# Revit family: Скамейка стальная круглая «Радиус Раунд» без спинки Арт 22157
name_source: partatom
category: Антураж
revit_build: Autodesk Revit 2018 (Build: 20180423_1000(x64)
units: mm (PartAtom-declared; Revit-internal decimal feet)

## family parameters
Всегда вертикально = Да
Источник визуального образа = Геометрия семейства
На основе рабочей плоскости = Нет
Общий = Нет
При загрузке вырезать с полостями = Нет
Точка расчета площади = Нет

## types (2) — shared parameters
URL = https://hobbyka.ru
Артикул товара = Арт. 22157
Высота = 450 мм
Группа модели = Скамейки
Изготовитель = ООО «Хоббика»
Изображение типоразмера = Скамейка стальная круглая «Радиус Раунд» без спинки Арт 22157.jpg
Материал изделия = Сталь, дерево
Цвет основания = Сталь
Цвет отделки = Дерево
Ширина = 500 мм

## per-type parameters (varying)
| type | Версия 2000 | Версия 2600 | Длина | Кол-во реек (условно) | Описание | Радиус |
| Версия R 2600 | Нет | Да | 16336 мм | 200 | Скамейка стальная круглая «Радиус Раунд» без спинки. Версия R 2600 | 2600 мм |
| Версия R 2000 | Да | Нет | 12566 мм | 175 | Скамейка стальная круглая «Радиус Раунд» без спинки. Версия R 2000 | 2000 мм |
